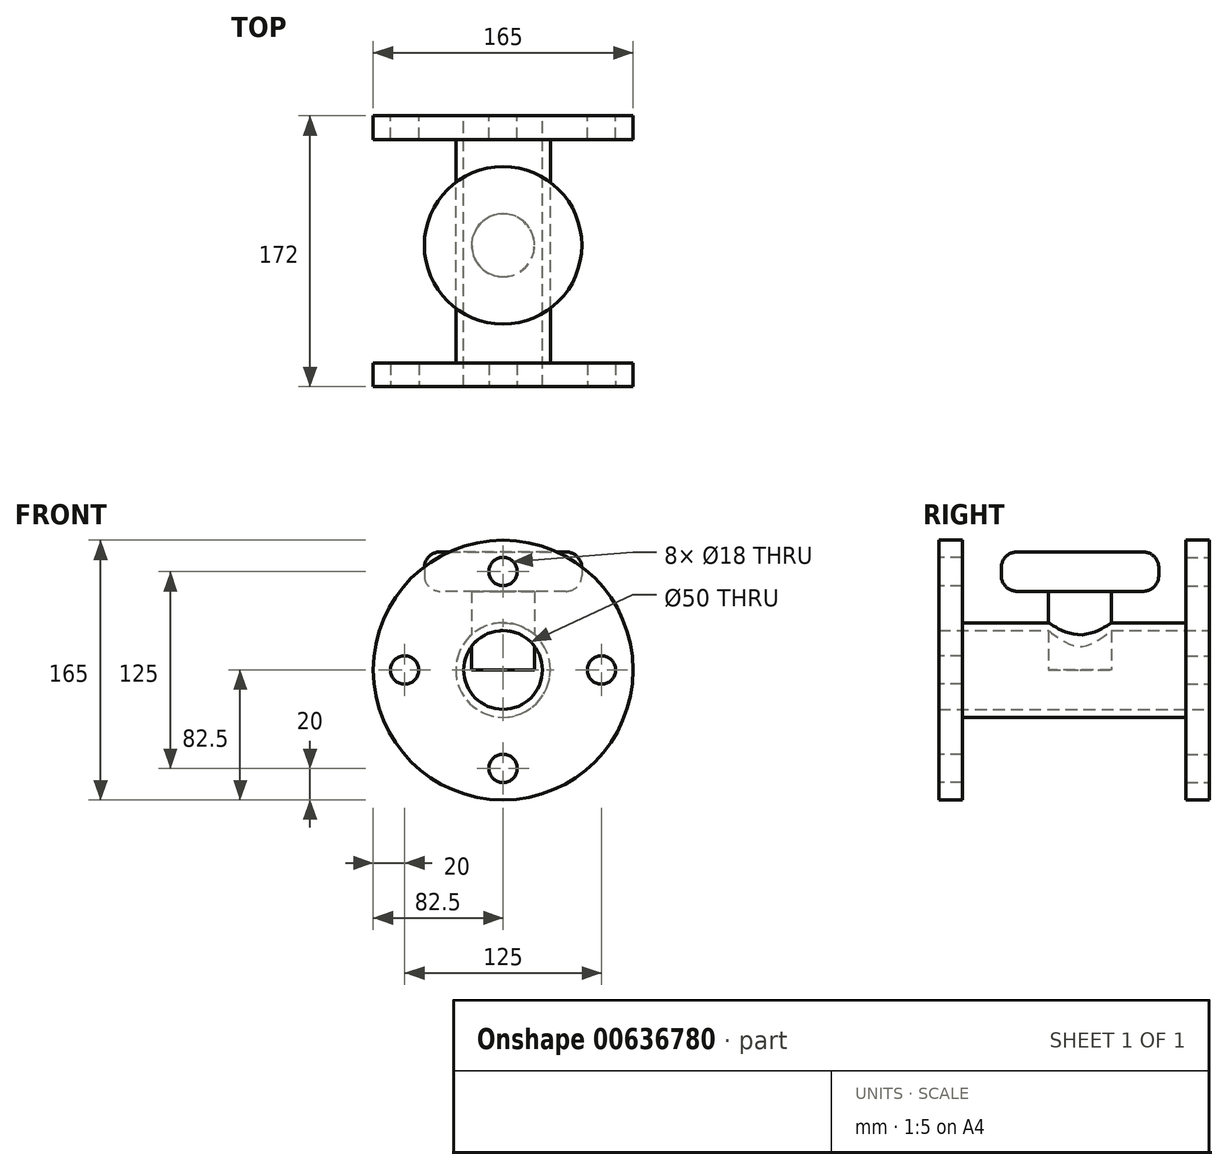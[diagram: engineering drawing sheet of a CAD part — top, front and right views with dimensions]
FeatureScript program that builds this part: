
annotation { "Feature Type Name" : "Feature", "Feature Type Description" : "" }
export const myFeature = defineFeature(function(context is Context, id is Id, definition is map)
    precondition{}
    {
        {
            var Q0;
            Q0=qCreatedBy(makeId("Front.planeOp"),FACE);
            var sketch = newSketch(context, id + "F0", { "sketchPlane" : qUnion([Q0])});
            skCircle(sketch, "E0", {"center": v(0, 0) * mm, "radius": 30 * mm});
            skCircle(sketch, "E1", {"center": v(0, 0) * mm, "radius": 25 * mm});
            skSolve(sketch);
        }
        {
            var Q0;
            Q0=makeQuery(id+"F0.imprint","IMPRINT",FACE,{"disambiguationData":[TD([[makeQuery(id+"F0.imprint","IMPRINT",EDGE,{"derivedFrom":sQuery(id+"F0.wireOp",EDGE,"E0")}),1.0]])]});
            extrude(context, id + "F1", {"entities" : qUnion([Q0]), "depth" : 172 * mm, "offsetDistance" : 25 * mm});
        }
        {
            var Q0;
            Q0=makeQuery(id+"F1.opExtrude","CAP_FACE",FACE,{"disambiguationData":[OSD([sQuery(id+"F0.wireOp",EDGE,"E0"),sQuery(id+"F0.wireOp",EDGE,"E1")])],"isStart":false});
            var sketch = newSketch(context, id + "F2", { "sketchPlane" : qUnion([Q0])});
            skCircle(sketch, "E2", {"center": v(0, 0) * mm, "radius": 82.5 * mm});
            skCircle(sketch, "E3", {"center": v(0, 62.5) * mm, "radius": 9 * mm});
            skCircle(sketch, "E4.1.0", {"center": v(-62.5, 0) * mm, "radius": 9 * mm});
            skCircle(sketch, "E4.2.0", {"center": v(0, -62.5) * mm, "radius": 9 * mm});
            skCircle(sketch, "E4.3.0", {"center": v(62.5, 0) * mm, "radius": 9 * mm});
            skSolve(sketch);
        }
        {
            var Q0;
            Q0=makeQuery(id+"F2.imprint","IMPRINT",FACE,{"disambiguationData":[TD([[makeQuery(id+"F2.imprint","IMPRINT",EDGE,{"derivedFrom":sQuery(id+"F2.wireOp",EDGE,"E2")}),1.0]])]});
            extrude(context, id + "F3", {"entities" : qUnion([Q0]), "operationType" : NewBodyOperationType.ADD, "oppositeDirection" : true, "depth" : 15 * mm, "offsetDistance" : 25 * mm});
        }
        {
            var Q0;
            Q0=makeQuery(id+"F1.opExtrude","CAP_FACE",FACE,{"disambiguationData":[OSD([sQuery(id+"F0.wireOp",EDGE,"E0"),sQuery(id+"F0.wireOp",EDGE,"E1")])],"isStart":true});
            var sketch = newSketch(context, id + "F4", { "sketchPlane" : qUnion([Q0])});
            skCircle(sketch, "E5.0", {"center": v(0, 0) * mm, "radius": 82.5 * mm});
            skCircle(sketch, "E6.0", {"center": v(0, 62.5) * mm, "radius": 9 * mm});
            skCircle(sketch, "E7.0", {"center": v(-62.5, 0) * mm, "radius": 9 * mm});
            skCircle(sketch, "E8.0", {"center": v(0, -62.5) * mm, "radius": 9 * mm});
            skCircle(sketch, "E9.0", {"center": v(62.5, 0) * mm, "radius": 9 * mm});
            skSolve(sketch);
        }
        {
            var Q0;
            Q0=makeQuery(id+"F4.imprint","IMPRINT",FACE,{"disambiguationData":[TD([[makeQuery(id+"F4.imprint","IMPRINT",EDGE,{"derivedFrom":sQuery(id+"F4.wireOp",EDGE,"E5.0")}),1.0]])]});
            extrude(context, id + "F5", {"entities" : qUnion([Q0]), "operationType" : NewBodyOperationType.ADD, "oppositeDirection" : true, "depth" : 15 * mm, "offsetDistance" : 25 * mm});
        }
        {
            var Q0;
            Q0=qCreatedBy(makeId("Top.planeOp"),FACE);
            var sketch = newSketch(context, id + "F6", { "sketchPlane" : qUnion([Q0])});
            skCircle(sketch, "E10", {"center": v(0, -82.26) * mm, "radius": 20 * mm});
            skSolve(sketch);
        }
        {
            var Q0;
            Q0 = qSketchRegion(id + "F6", true);
            extrude(context, id + "F7", {"entities" : qUnion([Q0]), "operationType" : NewBodyOperationType.ADD, "depth" : 50 * mm, "offsetDistance" : 25 * mm});
        }
        {
            var Q0;
            Q0=makeQuery(id+"F7.opExtrude","CAP_FACE",FACE,{"disambiguationData":[OSD([sQuery(id+"F6.wireOp",EDGE,"E10")])],"isStart":false});
            var sketch = newSketch(context, id + "F8", { "sketchPlane" : qUnion([Q0])});
            skCircle(sketch, "E11", {"center": v(0, -82.26) * mm, "radius": 50 * mm});
            skSolve(sketch);
        }
        {
            var Q0;
            Q0=makeQuery(id+"F8.imprint","IMPRINT",FACE,{"disambiguationData":[TD([[makeQuery(id+"F8.imprint","IMPRINT",EDGE,{"derivedFrom":sQuery(id+"F8.wireOp",EDGE,"E11")}),1.0]])]});
            var Q1;
            Q1=makeQuery(id+"F8.imprint","IMPRINT",FACE,{"disambiguationData":[TD([[makeQuery(id+"F8.imprint","IMPRINT",EDGE,{"derivedFrom":makeQuery(id+"F7.opExtrude","CAP_EDGE",EDGE,{"disambiguationData":[OSD([sQuery(id+"F6.wireOp",EDGE,"E10")])],"isStart":false})}),1.0]])]});
            extrude(context, id + "F9", {"entities" : qUnion([Q0, Q1]), "operationType" : NewBodyOperationType.ADD, "depth" : 25 * mm, "offsetDistance" : 25 * mm});
        }
        {
            var Q0;
            Q0=makeQuery(id+"F9.opExtrude","CAP_EDGE",EDGE,{"disambiguationData":[OSD([sQuery(id+"F8.wireOp",EDGE,"E11")])],"isStart":false});
            var Q1;
            Q1=makeQuery(id+"F9.opExtrude","CAP_EDGE",EDGE,{"disambiguationData":[OSD([sQuery(id+"F8.wireOp",EDGE,"E11")])],"isStart":true});
            fillet(context, id + "F10", {"entities" : qUnion([Q0, Q1]), "radius" : 10 * mm, "tangentPropagation" : true, "allowEdgeOverflow" : false});
        }
    });
